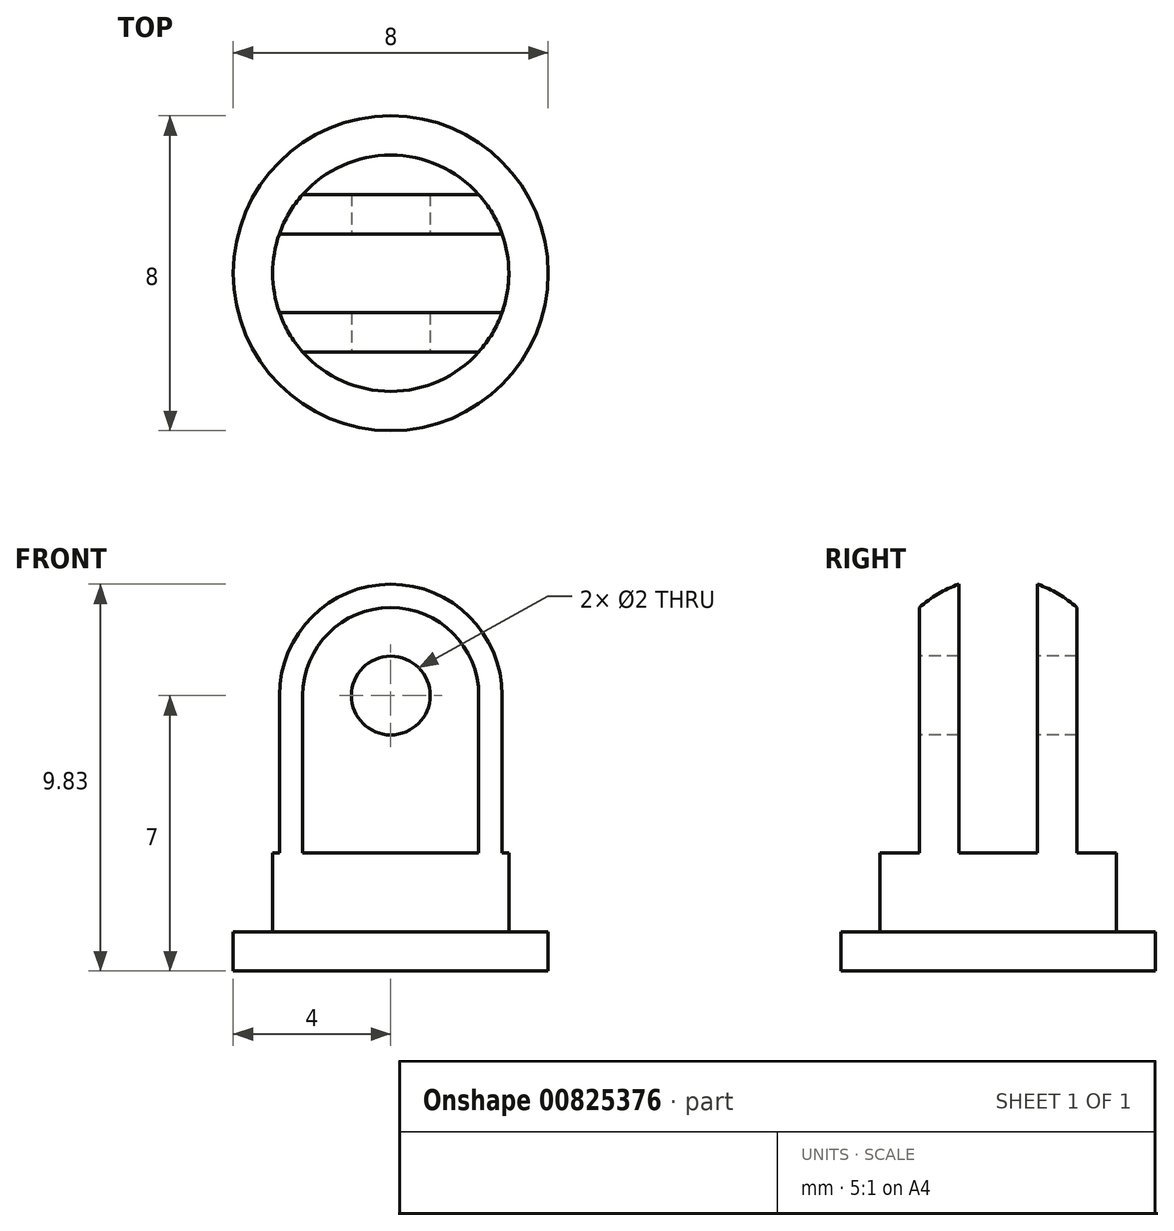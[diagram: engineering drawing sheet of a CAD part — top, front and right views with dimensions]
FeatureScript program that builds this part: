
annotation { "Feature Type Name" : "Feature", "Feature Type Description" : "" }
export const myFeature = defineFeature(function(context is Context, id is Id, definition is map)
    precondition{}
    {
        {
            var Q0;
            Q0=qCreatedBy(makeId("Top.planeOp"),FACE);
            var sketch = newSketch(context, id + "F0", { "sketchPlane" : qUnion([Q0])});
            skCircle(sketch, "E0", {"center": v(0, 0) * mm, "radius": 4 * mm});
            skSolve(sketch);
        }
        {
            var Q0;
            Q0 = qSketchRegion(id + "F0", true);
            extrude(context, id + "F1", {"entities" : qUnion([Q0]), "depth" : 1 * mm, "offsetDistance" : 25 * mm});
        }
        {
            var Q0;
            Q0=makeQuery(id+"F1.opExtrude","CAP_FACE",FACE,{"disambiguationData":[OSD([sQuery(id+"F0.wireOp",EDGE,"E0")])],"isStart":false});
            var sketch = newSketch(context, id + "F2", { "sketchPlane" : qUnion([Q0])});
            skCircle(sketch, "E1", {"center": v(0, 0) * mm, "radius": 3 * mm});
            skSolve(sketch);
        }
        {
            var Q0;
            Q0 = qSketchRegion(id + "F2", true);
            extrude(context, id + "F3", {"entities" : qUnion([Q0]), "operationType" : NewBodyOperationType.ADD, "depth" : 9 * mm, "offsetDistance" : 25 * mm});
        }
        {
            var Q0;
            Q0=makeQuery(id+"F3.opExtrude","CAP_EDGE",EDGE,{"disambiguationData":[OSD([sQuery(id+"F2.wireOp",EDGE,"E1")])],"isStart":false});
            fillet(context, id + "F4", {"entities" : qUnion([Q0]), "radius" : 3 * mm, "tangentPropagation" : true, "allowEdgeOverflow" : false});
        }
        {
            var Q0;
            Q0=qCreatedBy(makeId("Right.planeOp"),FACE);
            var sketch = newSketch(context, id + "F5", { "sketchPlane" : qUnion([Q0])});
            skLineSegment(sketch, "E2", {"start": v(0, 0) * mm, "end": v(0, 3) * mm, "construction": true});
            skLineSegment(sketch, "E3.bottom", {"start": v(0, 3) * mm, "end": v(1, 3) * mm});
            skLineSegment(sketch, "E3.top", {"start": v(0, 11.18) * mm, "end": v(1, 11.18) * mm});
            skLineSegment(sketch, "E3.right", {"start": v(1, 3) * mm, "end": v(1, 11.18) * mm});
            skLineSegment(sketch, "E4.bottom", {"start": v(0, 3) * mm, "end": v(-1, 3) * mm});
            skLineSegment(sketch, "E4.top", {"start": v(0, 11.18) * mm, "end": v(-1, 11.18) * mm});
            skLineSegment(sketch, "E4.right", {"start": v(-1, 3) * mm, "end": v(-1, 11.18) * mm});
            skLineSegment(sketch, "E5", {"start": v(-1, 3) * mm, "end": v(-2, 3) * mm, "construction": true});
            skLineSegment(sketch, "E6.bottom", {"start": v(-2, 3) * mm, "end": v(-4.97, 3) * mm});
            skLineSegment(sketch, "E6.top", {"start": v(-2, 11.15) * mm, "end": v(-4.97, 11.15) * mm});
            skLineSegment(sketch, "E6.left", {"start": v(-2, 3) * mm, "end": v(-2, 11.15) * mm});
            skLineSegment(sketch, "E6.right", {"start": v(-4.97, 3) * mm, "end": v(-4.97, 11.15) * mm});
            skLineSegment(sketch, "E7.MirrorCS", {"start": v(4.97, 3) * mm, "end": v(4.97, 11.15) * mm});
            skLineSegment(sketch, "E8.MirrorCS", {"start": v(2, 11.15) * mm, "end": v(4.97, 11.15) * mm});
            skLineSegment(sketch, "E9.MirrorCS", {"start": v(2, 3) * mm, "end": v(2, 11.15) * mm});
            skLineSegment(sketch, "E10.MirrorCS", {"start": v(2, 3) * mm, "end": v(4.97, 3) * mm});
            skSolve(sketch);
        }
        {
            var Q0;
            Q0 = qSketchRegion(id + "F5", true);
            extrude(context, id + "F6", {"entities" : qUnion([Q0]), "operationType" : NewBodyOperationType.REMOVE, "endBound" : BoundingType.SYMMETRIC, "depth" : 25 * mm, "offsetDistance" : 25 * mm});
        }
        {
            var Q0;
            Q0=makeQuery(id+"F6.boolean.opBoolean","COPY",FACE,{"derivedFrom":makeQuery(id+"F6.opExtrude","SWEPT_FACE",FACE,{"disambiguationData":[OSD([sQuery(id+"F5.wireOp",EDGE,"E6.left")])]})});
            var sketch = newSketch(context, id + "F7", { "sketchPlane" : qUnion([Q0])});
            skCircle(sketch, "E11", {"center": v(0, 7) * mm, "radius": 1 * mm});
            skSolve(sketch);
        }
        {
            var Q0;
            Q0 = qSketchRegion(id + "F7", true);
            extrude(context, id + "F8", {"entities" : qUnion([Q0]), "operationType" : NewBodyOperationType.REMOVE, "endBound" : BoundingType.THROUGH_ALL, "oppositeDirection" : true, "depth" : 25 * mm, "offsetDistance" : 25 * mm});
        }
    });
